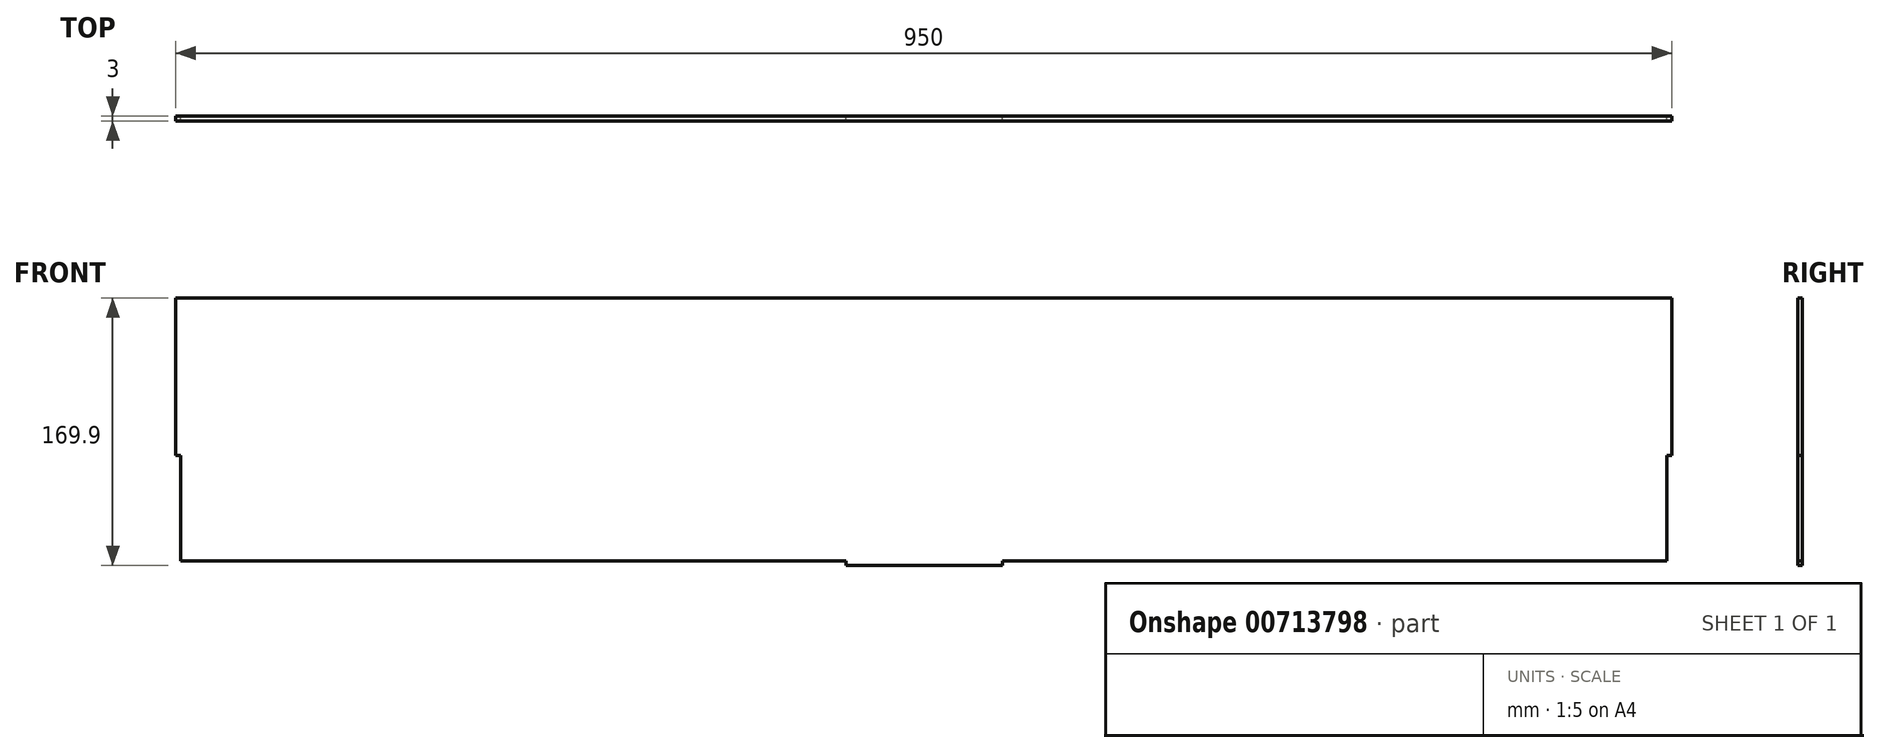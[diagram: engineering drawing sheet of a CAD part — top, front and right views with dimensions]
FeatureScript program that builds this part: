
annotation { "Feature Type Name" : "Feature", "Feature Type Description" : "" }
export const myFeature = defineFeature(function(context is Context, id is Id, definition is map)
    precondition{}
    {
        {
            var Q0;
            Q0=qCreatedBy(makeId("Front.planeOp"),FACE);
            var sketch = newSketch(context, id + "F0", { "sketchPlane" : qUnion([Q0])});
            skLineSegment(sketch, "E0.bottom", {"start": v(-475, 116.5) * mm, "end": v(475, 116.5) * mm});
            skPoint(sketch, "E0.middle", {"position": v(0, 0) * mm});
            skLineSegment(sketch, "E1.top", {"start": v(475, 16.5) * mm, "end": v(472, 16.5) * mm});
            skLineSegment(sketch, "E1.right", {"start": v(472, -50.5) * mm, "end": v(472, 16.5) * mm});
            skLineSegment(sketch, "E2.top", {"start": v(-475, 16.5) * mm, "end": v(-472, 16.5) * mm});
            skLineSegment(sketch, "E2.right", {"start": v(-472, -50.5) * mm, "end": v(-472, 16.5) * mm});
            skLineSegment(sketch, "E3.top", {"start": v(50, -53.4) * mm, "end": v(-49.5, -53.4) * mm});
            skLineSegment(sketch, "E3.left", {"start": v(50, -50.5) * mm, "end": v(50, -53.4) * mm});
            skLineSegment(sketch, "E3.right", {"start": v(-49.5, -50.5) * mm, "end": v(-49.5, -53.4) * mm});
            skLineSegment(sketch, "E4", {"start": v(-475, 16.5) * mm, "end": v(-475, 116.5) * mm});
            skLineSegment(sketch, "E5", {"start": v(-472, -50.5) * mm, "end": v(-49.5, -50.5) * mm});
            skLineSegment(sketch, "E6", {"start": v(472, -50.5) * mm, "end": v(50, -50.5) * mm});
            skLineSegment(sketch, "E7", {"start": v(475, 116.5) * mm, "end": v(475, 16.5) * mm});
            skSolve(sketch);
        }
        {
            var Q0;
            Q0=makeQuery(id+"F0.imprint","IMPRINT",FACE,{"disambiguationData":[TD([[makeQuery(id+"F0.imprint","IMPRINT",EDGE,{"derivedFrom":sQuery(id+"F0.wireOp",EDGE,"E0.bottom")}),-1.0]])]});
            extrude(context, id + "F1", {"entities" : qUnion([Q0]), "depth" : 3 * mm, "offsetDistance" : 25 * mm});
        }
    });
